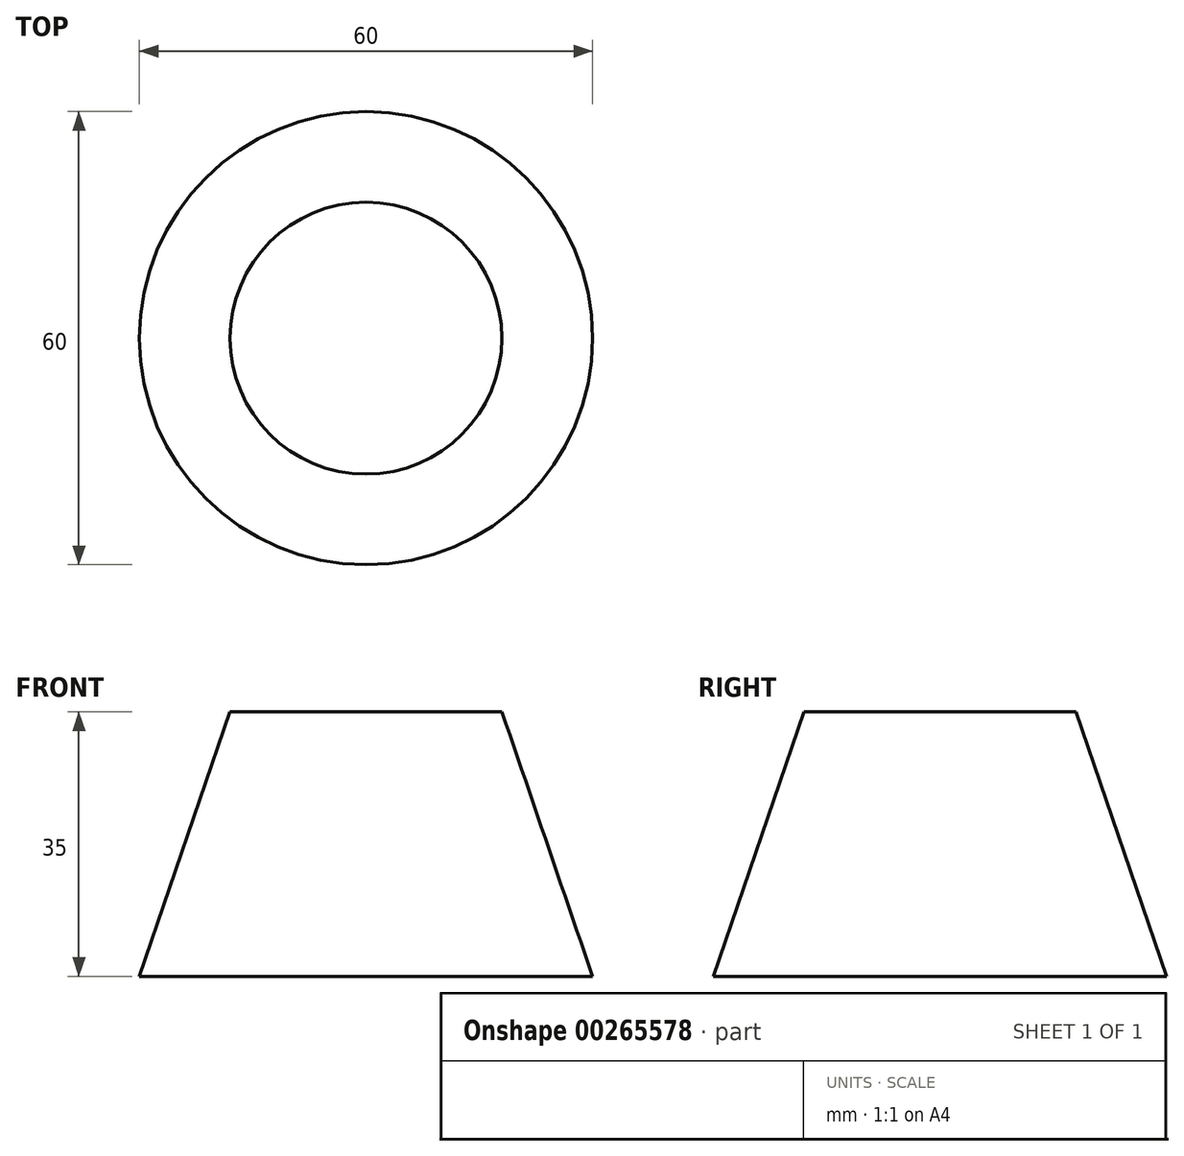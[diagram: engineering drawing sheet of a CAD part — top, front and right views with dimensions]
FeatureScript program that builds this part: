
annotation { "Feature Type Name" : "Feature", "Feature Type Description" : "" }
export const myFeature = defineFeature(function(context is Context, id is Id, definition is map)
    precondition{}
    {
        {
            var Q0;
            Q0=qCreatedBy(makeId("Front.planeOp"),FACE);
            var sketch = newSketch(context, id + "F0", { "sketchPlane" : qUnion([Q0])});
            skLineSegment(sketch, "E0", {"start": v(0, 0) * mm, "end": v(0, 35) * mm});
            skLineSegment(sketch, "E1", {"start": v(0, 35) * mm, "end": v(18, 35) * mm});
            skLineSegment(sketch, "E2", {"start": v(18, 35) * mm, "end": v(30, 0) * mm});
            skLineSegment(sketch, "E3", {"start": v(30, 0) * mm, "end": v(0, 0) * mm});
            skLineSegment(sketch, "E4", {"start": v(0, 62.81) * mm, "end": v(0, -38.38) * mm});
            skSolve(sketch);
        }
        {
            var Q0;
            {var subQ0=sQuery(id+"F0.wireOp",EDGE,"E1");Q0=makeQuery(id+"F0.imprint","IMPRINT",FACE,{"disambiguationData":[TD([[makeQuery(id+"F0.imprint","IMPRINT",EDGE,{"derivedFrom":subQ0}),-1.0]])]});}
            var Q1;
            Q1=sQuery(id+"F0.wireOp",EDGE,"E4");
            revolve(context, id + "F1", {"entities" : qUnion([Q0]), "axis" : qUnion([Q1]), "revolveType" : RevolveType.FULL});
        }
    });
